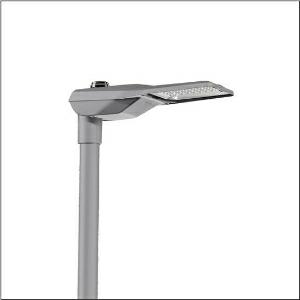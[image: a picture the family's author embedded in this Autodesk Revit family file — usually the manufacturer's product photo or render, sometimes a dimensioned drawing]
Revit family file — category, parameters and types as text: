
# Revit family: streetlight_sl_21_mini___p0_8a_5xe6u67n08hb_4629
name_source: partatom
category: Lighting Fixtures
units: mm (PartAtom-declared; Revit-internal decimal feet)

## family parameters
Cut with Voids When Loaded = No
Host = Face
Light Source = No
Part Type = Normal
Room Calculation Point = No
Round Connector Dimension = Use Diameter
Shared = No

## types (1)
- --- (1 x LED, 8180 lm, 66 W, 2700K)
    Apparent Load = 66 VA
    CIE Flux Codes = 33 69 96 100 100
    Color Rendering = 70
    Color Temperature = 2700K
    Default Elevation = 1800 mm
    Description = Streetlight SL 21 mini, mast luminaire, primary light control with lens, of PMMA, primary optical cover: cover, of toughened safety glass, transparent, light distribution: P0.8a, light emission: direct distribution, primary light characteristic: asymmetric, installation type: side-entry, LED, 3G 1.5mm², High Power LED, rated luminous flux: 8.180lm, luminous efficacy: 124lm/W, light colour: 727, colour temperature: 2700K, control gear: NEMA (7pin), control: flexible luminous flux parameterisation, time-dependent luminous flux control, constant luminous flux control, pre-setting: linear dimming characteristic, overheat protection, mains connection: 230..240V, AC, 50/60Hz, connection cable pre-assembled, cable length: 8,5m, wiring characteristics: H07RN-F, start of lifetime: 66W, end of service life: 69W, reduction: 30W, luminaire housing, of diecast aluminium (EN AC-44300), powder-coated, Siteco® metallic grey (DB 702S), corrosivity category C5 mid according to DIN EN ISO 12944, multi-level sealing system, sealing non-destructively replaceable, inclination adjustable: 0°, 5°, 10°, 15°, length: 628mm, width: 235mm, height: 110mm, spigot size: 42mm (side-entry), mounting height: 4..8m, protection rating (complete): IP66, insulation class (complete): insulation class I (protective earthing), certification: CE, ENEC, ENEC+, VDE, impact resistance: IK10, permissible operating ambient temperature for outdoor applications: -40..+50°C, standard-compliant lighting for roads and squares, packaging unit: 1 piece

Light Distribution: P0.8a
    Height = 110 mm
    Lamp = 1 x LED
    Lamp Light Flux = 8180 lm
    Lamp Power = 66 W
    Lamp count = 1
    Length = 625 mm
    Luminous efficacy = 124 lm/W
    Manufacturer = Siteco
    ModVariant = No
    Model = 5XE6U67N08HB
    Number of Poles = 1
    OnlyDefault = Yes
    Power Factor = 1
    Product Name = Streetlight SL 21 mini | P0.8a
    Product group = mast luminaire | pylon top
    ProductGroupID = 6100
    Protection Class = Protection class I
    Protection Degree = IP 66
    RLX_Detail_Level = 1
    RLX_Emergency_Light_Flux = 0 lm
    RLX_Emergency_Type = 0
    RLX_Emergency_Type_DB = No
    RlxData = <blob elided: 25865 chars, md5=081f3797>
    Socket = socket
    Standby Power = 0 W
    System Light Flux = 8180 lm
    System Power = 66 W
    Type Comments = factory setting: luminous flux: 100 % | dim-lin: 254 | 670 mA
    Type Image = l_1294379.jpg
    URL = http://relux.com
    VarID = @adj_073386
    Voltage = 0 V
    Weight = 0.00 kg
    Width = 234 mm

## geometry (parser evidence)
native form markers: Blend x4, Sweep x10
no freeform markers — native parametric forms only
